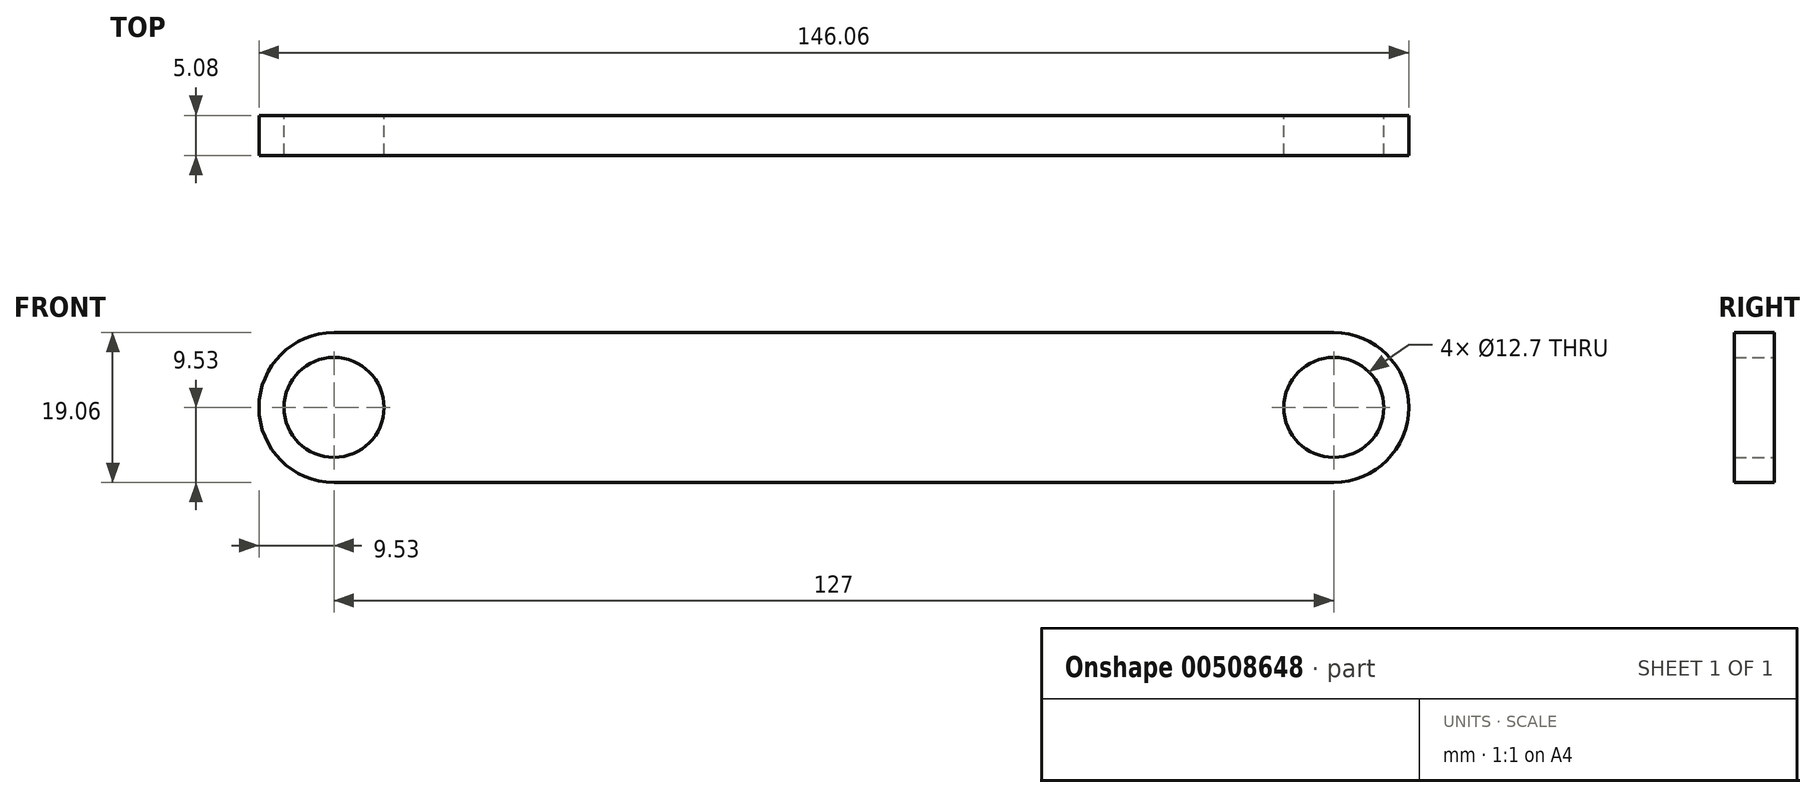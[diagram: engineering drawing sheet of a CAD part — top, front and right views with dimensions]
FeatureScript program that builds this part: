
annotation { "Feature Type Name" : "Feature", "Feature Type Description" : "" }
export const myFeature = defineFeature(function(context is Context, id is Id, definition is map)
    precondition{}
    {
        {
            var Q0;
            Q0=qCreatedBy(makeId("Front.planeOp"),FACE);
            var sketch = newSketch(context, id + "F0", { "sketchPlane" : qUnion([Q0])});
            skLineSegment(sketch, "E0", {"start": v(0, 0) * mm, "end": v(-57.15, 0) * mm});
            skLineSegment(sketch, "E1", {"start": v(0, 0) * mm, "end": v(57.15, 0) * mm});
            skCircle(sketch, "E2", {"center": v(-63.5, 0) * mm, "radius": 6.35 * mm});
            skCircle(sketch, "E3", {"center": v(63.5, 0) * mm, "radius": 6.35 * mm});
            skCircle(sketch, "E4", {"center": v(-63.5, 0) * mm, "radius": 9.53 * mm});
            skCircle(sketch, "E5", {"center": v(63.5, 0) * mm, "radius": 9.53 * mm});
            skLineSegment(sketch, "E6.bottom", {"start": v(-63.5, 0) * mm, "end": v(63.5, 0) * mm});
            skLineSegment(sketch, "E6.top", {"start": v(-63.5, 9.52) * mm, "end": v(63.5, 9.52) * mm});
            skLineSegment(sketch, "E6.left", {"start": v(-63.5, 0) * mm, "end": v(-63.5, 9.52) * mm});
            skLineSegment(sketch, "E6.right", {"start": v(63.5, 0) * mm, "end": v(63.5, 9.52) * mm});
            skLineSegment(sketch, "E7.top", {"start": v(-63.5, -9.52) * mm, "end": v(63.5, -9.52) * mm});
            skLineSegment(sketch, "E7.left", {"start": v(-63.5, 0) * mm, "end": v(-63.5, -9.52) * mm});
            skLineSegment(sketch, "E7.right", {"start": v(63.5, 0) * mm, "end": v(63.5, -9.52) * mm});
            skSolve(sketch);
        }
        {
            var Q0;
            Q0 = qSketchRegion(id + "F0", true);
            extrude(context, id + "F1", {"entities" : qUnion([Q0]), "depth" : 5.08 * mm});
        }
    });
